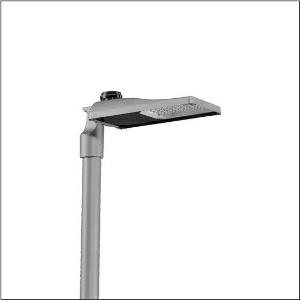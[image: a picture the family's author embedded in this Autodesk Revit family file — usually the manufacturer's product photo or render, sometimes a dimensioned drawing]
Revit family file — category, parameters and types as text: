
# Revit family: streetlight_sl_31_mini___st1_0a_5xh6d35n08ga_9230
name_source: partatom
category: Lighting Fixtures
units: mm (PartAtom-declared; Revit-internal decimal feet)

## family parameters
Cut with Voids When Loaded = No
Host = Face
Light Source = No
Part Type = Normal
Room Calculation Point = No
Round Connector Dimension = Use Diameter
Shared = No

## types (1)
- --- (1 x LED, 5710 lm, 37.3 W, 3000K)
    Apparent Load = 37 VA
    CIE Flux Codes = 37 72 97 100 100
    Color Rendering = 70
    Color Temperature = 3000K
    Default Elevation = 1800 mm
    Description = Streetlight SL 31 mini NEMA (7pin), Desk-Remote mast luminaire for post-top, side-entry; light control with lens of PMMA; light distribution: ST1.0a, direct asymmetric distribution, for standard-compliant lighting for roads and squares; LED: luminous flux: 5.710lm, light colour: 730, colour temperature: 3000K; luminous efficacy: 153,1lm/W; control: pre-setting: linear dimming characteristic, flexible luminous flux parameterisation, time-dependent luminous flux control, constant luminous flux control, intelligent temperature release in ECG and LED module, overheat protection; luminaire housing, of diecast aluminium, Siteco® metallic grey (DB 702S), corrosivity category C5 high according to DIN EN ISO 12944; cover of toughened safety glass, transparent, opened without tools; mast flange of diecast aluminium, Siteco® metallic grey (DB 702S), spigot size: 76/60mm, mast flange included unmounted; with cable H07RN-F 3x 1.5mm², cable length: 6,5m, connection cable pre-assembled; mains connection: 220..240V, AC, 50/60Hz; power consumption (at start of service life): 37,3W / (at end of service life): 38,7W / (with reduced operation 50%): 17,5W; protection rating (complete): IP66; insulation class (complete): insulation class I (protective earthing); impact resistance: IK10; certification: CE, ENEC, ENEC+, VDE, UKCA; permissible operating ambient temperature for outdoor applications: -40..+50°C; packaging unit: 1 piece

Light Distribution: ST1.0a
    Height = 76 mm
    Lamp = 1 x LED
    Lamp Light Flux = 5710 lm
    Lamp Power = 37.3 W
    Lamp count = 1
    Length = 547 mm
    Luminous efficacy = 153 lm/W
    Manufacturer = Siteco
    ModVariant = No
    Model = 5XH6D35N08GA
    Number of Poles = 1
    OnlyDefault = Yes
    Power Factor = 1
    Product Name = Streetlight SL 31 mini | ST1.0a
    Product group = mast luminaire | pylon top
    ProductGroupID = 6100
    Protection Class = Protection class I
    Protection Degree = IP 66
    RLX_Detail_Level = 1
    RLX_Emergency_Light_Flux = 0 lm
    RLX_Emergency_Type = 0
    RLX_Emergency_Type_DB = No
    RlxData = <blob elided: 40293 chars, md5=16d41f86>
    Socket = socket
    Standby Power = 0 W
    System Light Flux = 5710 lm
    System Power = 37 W
    Type Comments = factory setting: luminous flux: 100 % | dim-lin: 254 | 386 mA
    Type Image = l_1300322.jpg
    URL = http://relux.com
    VarID = @adj_074227
    Voltage = 0 V
    Weight = 0.00 kg
    Width = 265 mm

## geometry (parser evidence)
native form markers: Blend x4, Sweep x9
no freeform markers — native parametric forms only
